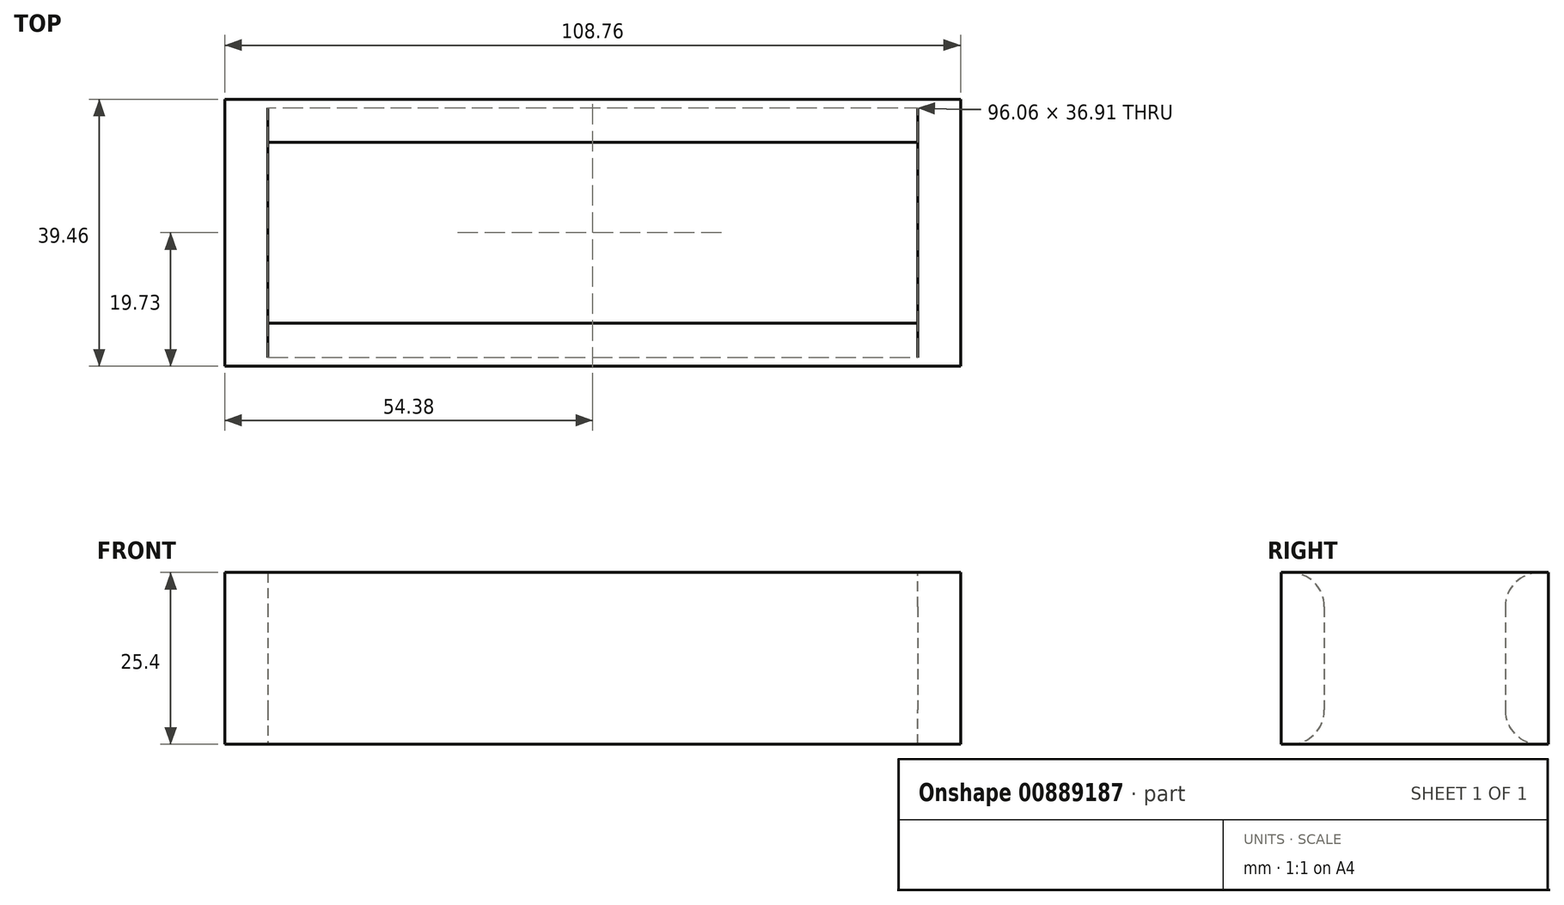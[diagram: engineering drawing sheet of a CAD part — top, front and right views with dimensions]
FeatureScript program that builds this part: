
annotation { "Feature Type Name" : "Feature", "Feature Type Description" : "" }
export const myFeature = defineFeature(function(context is Context, id is Id, definition is map)
    precondition{}
    {
        {
            var Q0;
            Q0=qCreatedBy(makeId("Top.planeOp"),FACE);
            var sketch = newSketch(context, id + "F0", { "sketchPlane" : qUnion([Q0])});
            skLineSegment(sketch, "E0.bottom", {"start": v(48.03, 13.38) * mm, "end": v(-48.03, 13.38) * mm});
            skLineSegment(sketch, "E0.top", {"start": v(48.03, -13.38) * mm, "end": v(-48.03, -13.38) * mm});
            skLineSegment(sketch, "E0.left", {"start": v(48.03, 13.38) * mm, "end": v(48.03, -13.38) * mm});
            skLineSegment(sketch, "E0.right", {"start": v(-48.03, 13.38) * mm, "end": v(-48.03, -13.38) * mm});
            skPoint(sketch, "E0.middle", {"position": v(0, 0) * mm});
            skLineSegment(sketch, "E1.0", {"start": v(54.38, 19.73) * mm, "end": v(-54.38, 19.73) * mm});
            skLineSegment(sketch, "E1.1", {"start": v(54.38, 19.73) * mm, "end": v(54.38, -19.73) * mm});
            skLineSegment(sketch, "E1.2", {"start": v(54.38, -19.73) * mm, "end": v(-54.38, -19.73) * mm});
            skLineSegment(sketch, "E1.3", {"start": v(-54.38, 19.73) * mm, "end": v(-54.38, -19.73) * mm});
            skSolve(sketch);
        }
        {
            var Q0;
            Q0 = qSketchRegion(id + "F0", true);
            extrude(context, id + "F1", {"entities" : qUnion([Q0]), "depth" : 25.4 * mm, "offsetDistance" : 25.4 * mm});
        }
        {
            var Q0;
            Q0=makeQuery(id+"F1.opExtrude","CAP_EDGE",EDGE,{"disambiguationData":[OSD([sQuery(id+"F0.wireOp",EDGE,"E0.bottom")])],"isStart":false});
            var Q1;
            Q1=makeQuery(id+"F1.opExtrude","CAP_EDGE",EDGE,{"disambiguationData":[OSD([sQuery(id+"F0.wireOp",EDGE,"E0.bottom")])],"isStart":true});
            var Q2;
            Q2=makeQuery(id+"F1.opExtrude","CAP_EDGE",EDGE,{"disambiguationData":[OSD([sQuery(id+"F0.wireOp",EDGE,"E0.top")])],"isStart":true});
            var Q3;
            Q3=makeQuery(id+"F1.opExtrude","CAP_EDGE",EDGE,{"disambiguationData":[OSD([sQuery(id+"F0.wireOp",EDGE,"E0.top")])],"isStart":false});
            fillet(context, id + "F2", {"entities" : qUnion([Q0, Q1, Q2, Q3]), "radius" : 5.08 * mm, "tangentPropagation" : true, "allowEdgeOverflow" : false});
        }
    });
